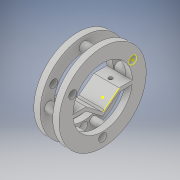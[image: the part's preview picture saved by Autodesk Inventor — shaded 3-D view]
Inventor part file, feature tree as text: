
AUTODESK INVENTOR PART (.ipt)
format: ipt  version: 2019 (Build 230136000, 136)  size: 260,608 bytes
history: native  units: in
note: dims shown in document units (in); Inventor stores cm internally (conversion verified against a paired STEP export)
features: sketch x9, extrude x7, mirror x2, fillet x2, projected_geometry x2, plane x1, pattern_circular x1
ambient origin geometry x8: Origin, YZ Plane, XZ Plane, XY Plane, X Axis, Y Axis, Z Axis, Center Point
bodies: Solid1 (feature_tree)
feature tree (24):
  extrude  "Extrusion1"  Depth=0.4331in
  extrude  "Extrusion2"  Depth=0.3937in
  mirror  "Mirror1"
  extrude  "Extrusion3"  Depth=0.5118in
  plane  "Work Plane1"
  extrude  "Extrusion4"  Depth=0.1181in
  extrude  "Extrusion5"  Depth=0.7874in TaperAngle=0.0deg
  pattern_circular  "Circular Pattern1"  Count=2  [1 undecoded]
  extrude  "Extrusion6"  Depth=0.1969in TaperAngle=0.0deg
  extrude  "Extrusion7"  Depth=0.7874in
  mirror  "Mirror2"
  sketch  "Sketch12"  dims[d39=2.1654in]
  sketch  "Sketch14"  dims[d40=0.2756in d41=0.1969in d42=0.1969in d43=0.2756in d44=0.2756in d45=0.7874in d46=0.0in d47=0.122in d48=0.1969in d49=0.0in d50=0.4724in d51=0.0787in d52=90.0deg d53=0.122in d54=0.0787in d55=0.0787in]
  fillet  "Fillet1"  Radius=0.7874in
  fillet  "Fillet2"  Radius=1.1811in
  sketch  "Sketch2"  dims[d4=2.7165in d5=0.4331in]
  sketch  "Sketch4"  dims[d6=0.1969in d7=0.0in d16=0.3937in]
  sketch  "Sketch5"  dims[d17=0.5118in d18=0.3603in]
  projected_geometry  "Projected Loop1"
  sketch  "Sketch6"  dims[d20=0.1181in d21=0.1181in]
  projected_geometry  "Projected Loop2"
  sketch  "Sketch9"  dims[d22=180.0deg d23=0.7874in d24=0.0in d25=0.7874in d26=0.0in]
  sketch  "Sketch10"  dims[d27=-0.7874in d28=0.1969in d29=0.0in]
  sketch  "Sketch11"  dims[d32=2.1654in d33=0.2441in d34=0.7874in d35=0.0in d36=1.1811in d37=360.0deg]
note: 1 required parameter value undecoded (feature->parameter linkage not recoverable at this tier; creation-order binding heuristic only, values carry confidence <= 0.55)
